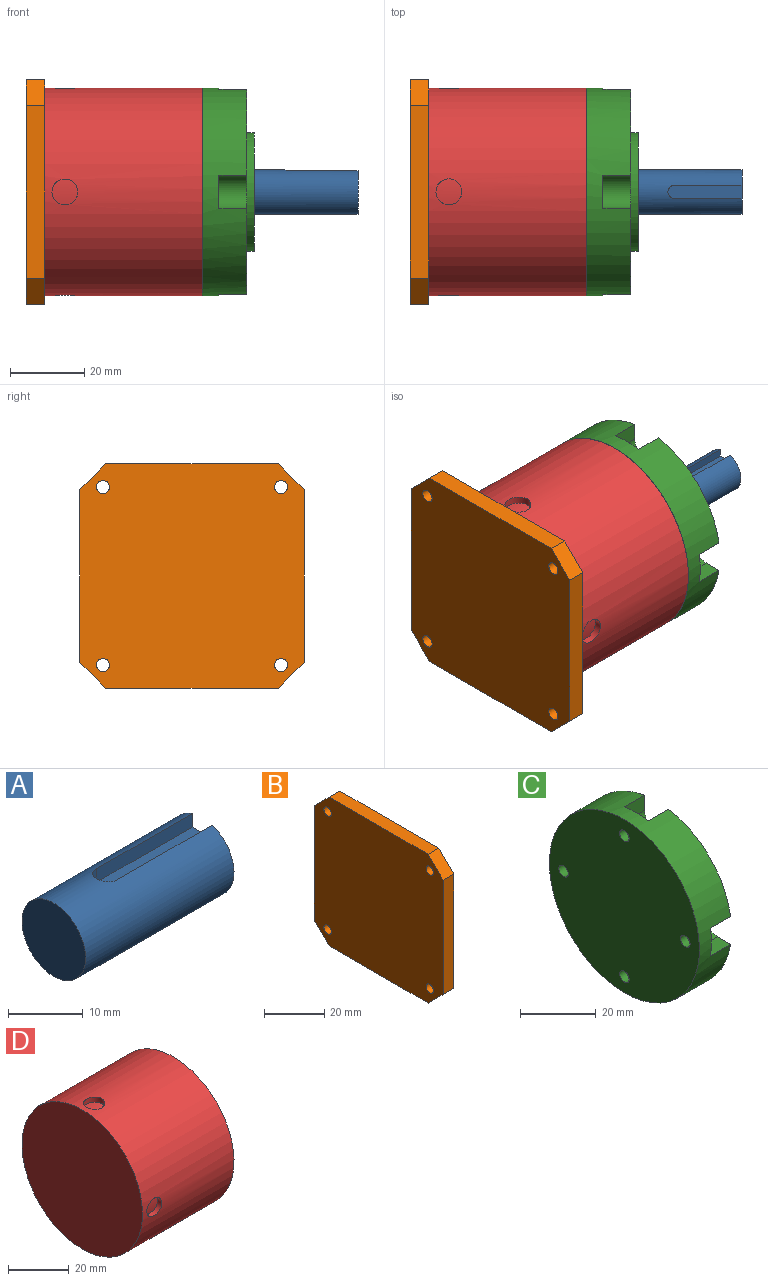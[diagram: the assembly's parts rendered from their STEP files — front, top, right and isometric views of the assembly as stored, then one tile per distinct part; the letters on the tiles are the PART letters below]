
ASSEMBLY  parts=4 mates=3
PART A: 8 faces, bbox 28x12x12 mm
  f0: plane 12x11.7mm, normal (1,0,0), area 104.1mm2, adj f1,f3,f4,f5
  f1: cylinder r=6mm len=28mm, axis (-1,0,0), area 981.1mm2, adj f0,f2,f3,f5,f6,f7
  f2: plane 12x12mm, normal (-1,0,0), area 113.1mm2, adj f1
  f3: plane 18x2.2mm, normal (0,1,0), area 39.6mm2, adj f0,f1,f4,f6
  f4: plane 20x3.75mm, normal (0,0,1), area 73.3mm2, adj f0,f3,f5,f6,f7
  f5: plane 18x2.2mm, normal (0,-1,0), area 39.6mm2, adj f0,f1,f4,f7
  f6: cylinder r=2mm len=2.5mm, axis (0,0,-1), area 7.1mm2, adj f1,f3,f4,f7
  f7: cylinder r=2mm len=2.5mm, axis (0,0,1), area 7.1mm2, adj f1,f4,f5,f6
PART B: 14 faces, bbox 5x60.5x60.5 mm
  f0: plane 46.5x5mm, normal (0,0,1), area 232.5mm2, adj f8,f9,f10,f13
  f1: plane 46.5x5mm, normal (0,-1,0), area 232.5mm2, adj f8,f9,f12,f13
  f2: plane 46.5x5mm, normal (0,0,-1), area 232.5mm2, adj f8,f9,f11,f12
  f3: cylinder r=1.75mm len=5mm, axis (-1,0,0), area 55mm2, adj f8,f9
  f4: cylinder r=1.75mm len=5mm, axis (-1,0,0), area 55mm2, adj f8,f9
  f5: cylinder r=1.75mm len=5mm, axis (-1,0,0), area 55mm2, adj f8,f9
  f6: cylinder r=1.75mm len=5mm, axis (-1,0,0), area 55mm2, adj f8,f9
  f7: plane 46.5x5mm, normal (0,1,0), area 232.5mm2, adj f8,f9,f10,f11
  f8: plane 60.5x60.5mm, normal (1,0,0), area 3523.8mm2, adj f0,f1,f2,f3,f4,f5,f6,f7
  f9: plane 60.5x60.5mm, normal (-1,0,0), area 3523.8mm2, adj f0,f1,f2,f3,f4,f5,f6,f7
  f10: plane 7x7mm, normal (0,0.71,0.71), area 49.5mm2, adj f0,f7,f8,f9
  f11: plane 7x7mm, normal (0,0.71,-0.71), area 49.5mm2, adj f2,f7,f8,f9
  f12: plane 7x7mm, normal (0,-0.71,-0.71), area 49.5mm2, adj f1,f2,f8,f9
  f13: plane 7x7mm, normal (0,-0.71,0.71), area 49.5mm2, adj f0,f1,f8,f9
PART C: 33 faces, bbox 14x56x56 mm
  f0: cylinder r=1.75mm len=4.5mm, axis (1,0,0), area 49.5mm2, adj f6,f23
  f1: cylinder r=2.25mm len=7.5mm, axis (1,0,0), area 106mm2, adj f2,f21
  f2: plane 4.5x4.5mm, normal (1,0,0), area 15.9mm2, adj f1
  f3: plane 7.5x4.89mm, normal (0,0,-1), area 36.6mm2, adj f5,f6,f21,f22
  f4: plane 7.5x4.89mm, normal (0,0,1), area 36.6mm2, adj f5,f6,f21,f22
  f5: cylinder r=4.5mm len=9mm, axis (1,0,0), area 106mm2, adj f3,f4,f6,f21
  f6: plane 9.75x9mm, normal (1,0,0), area 68.3mm2, adj f0,f3,f4,f5,f22
  f7: cylinder r=1.75mm len=4.5mm, axis (1,0,0), area 49.5mm2, adj f13,f23
  f8: cylinder r=2.25mm len=7.5mm, axis (1,0,0), area 106mm2, adj f9,f21
  f9: plane 4.5x4.5mm, normal (1,0,0), area 15.9mm2, adj f8
  f10: plane 7.5x4.89mm, normal (0,1,0), area 36.6mm2, adj f12,f13,f21,f22
  f11: plane 7.5x4.89mm, normal (0,-1,0), area 36.6mm2, adj f12,f13,f21,f22
  f12: cylinder r=4.5mm len=9mm, axis (1,0,0), area 106mm2, adj f10,f11,f13,f21
  f13: plane 9.75x9mm, normal (1,0,0), area 68.3mm2, adj f7,f10,f11,f12,f22
  f14: cylinder r=1.75mm len=4.5mm, axis (1,0,0), area 49.5mm2, adj f20,f23
  f15: cylinder r=2.25mm len=7.5mm, axis (1,0,0), area 106mm2, adj f16,f21
  f16: plane 4.5x4.5mm, normal (1,0,0), area 15.9mm2, adj f15
  f17: plane 7.5x4.89mm, normal (0,0,1), area 36.6mm2, adj f19,f20,f21,f22
  f18: plane 7.5x4.89mm, normal (0,0,-1), area 36.6mm2, adj f19,f20,f21,f22
  f19: cylinder r=4.5mm len=9mm, axis (1,0,0), area 106mm2, adj f17,f18,f20,f21
  f20: plane 9.75x9mm, normal (1,0,0), area 68.3mm2, adj f14,f17,f18,f19,f22
  f21: plane 55.27x55.27mm, normal (1,0,0), area 1283.3mm2, adj f1,f3,f4,f5,f8,f10,f11,f12
  f22: cylinder r=28mm len=56mm, axis (-1,0,0), area 1840mm2, adj f3,f4,f6,f10,f11,f13,f17,f18
  f23: plane 56x56mm, normal (-1,0,0), area 2424.5mm2, adj f0,f7,f14,f22,f32
  f24: cylinder r=16mm len=32mm, axis (-1,0,0), area 201.1mm2, adj f21,f25
  f25: plane 32x32mm, normal (1,0,0), area 804.2mm2, adj f24
  f26: cylinder r=2.25mm len=7.5mm, axis (1,0,0), area 106mm2, adj f21,f27
  f27: plane 4.5x4.5mm, normal (1,0,0), area 15.9mm2, adj f26
  f28: plane 7.5x4.89mm, normal (0,1,0), area 36.6mm2, adj f21,f22,f29,f31
  f29: cylinder r=4.5mm len=9mm, axis (1,0,0), area 106mm2, adj f21,f28,f30,f31
  f30: plane 7.5x4.89mm, normal (0,-1,0), area 36.6mm2, adj f21,f22,f29,f31
  f31: plane 9.75x9mm, normal (1,0,0), area 68.3mm2, adj f22,f28,f29,f30,f32
  f32: cylinder r=1.75mm len=4.5mm, axis (1,0,0), area 49.5mm2, adj f23,f31
PART D: 19 faces, bbox 42.5x56x56 mm
  f0: cylinder r=28mm len=7mm, axis (-1,0,0), area 38.6mm2, adj f1
  f1: cylinder r=3.5mm len=7mm, axis (0,-1,0), area 44mm2, adj f0,f12
  f2: cylinder r=28mm len=7mm, axis (-1,0,0), area 38.6mm2, adj f3
  f3: cylinder r=3.5mm len=7mm, axis (0,0,-1), area 44mm2, adj f2,f12
  f4: cylinder r=28mm len=7mm, axis (-1,0,0), area 38.6mm2, adj f5
  f5: cylinder r=3.5mm len=7mm, axis (0,1,0), area 44mm2, adj f4,f12
  f6: plane 3.5x3.5mm, normal (1,0,0), area 9.6mm2, adj f7
  f7: cylinder r=1.75mm len=5mm, axis (1,0,0), area 55mm2, adj f6,f13
  f8: plane 3.5x3.5mm, normal (1,0,0), area 9.6mm2, adj f9
  f9: cylinder r=1.75mm len=5mm, axis (1,0,0), area 55mm2, adj f8,f13
  f10: plane 3.5x3.5mm, normal (1,0,0), area 9.6mm2, adj f11
  f11: cylinder r=1.75mm len=5mm, axis (1,0,0), area 55mm2, adj f10,f13
  f12: cylinder r=28mm len=56mm, axis (-1,0,0), area 7323.3mm2, adj f1,f3,f5,f13,f14,f17
  f13: plane 56x56mm, normal (1,0,0), area 2424.5mm2, adj f7,f9,f11,f12,f16
  f14: plane 56x56mm, normal (-1,0,0), area 2463mm2, adj f12
  f15: plane 3.5x3.5mm, normal (1,0,0), area 9.6mm2, adj f16
  f16: cylinder r=1.75mm len=5mm, axis (1,0,0), area 55mm2, adj f13,f15
  f17: cylinder r=3.5mm len=7mm, axis (0,0,1), area 44mm2, adj f12,f18
  f18: cylinder r=28mm len=7mm, axis (-1,0,0), area 38.6mm2, adj f17
PLACE A t=(-21.19,15.17,2.35)mm
PLACE B t=(-21.19,15.17,2.35)mm
PLACE C t=(-21.19,15.17,2.35)mm
PLACE D t=(-21.19,15.17,2.35)mm
MATE revolute A.f1 <-> C.f24  axis (-1,0,0) through (40.31,15.17,2.35)mm
MATE fastened D.f12 <-> B.f8  axis (-1,0,0) through (-16.19,15.17,2.35)mm
MATE fastened D.f12 <-> C.f22  axis (1,0,0) through (26.31,15.17,2.35)mm
